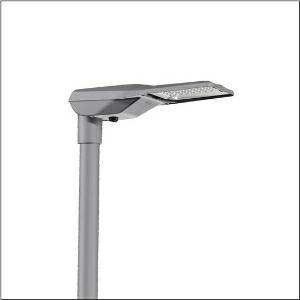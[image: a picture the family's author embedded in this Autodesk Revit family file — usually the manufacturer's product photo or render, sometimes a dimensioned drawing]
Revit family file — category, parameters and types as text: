
# Revit family: streetlight_sl_21_mini___p0_8a_5xe2u33r08hb_8bcd
name_source: partatom
category: Lighting Fixtures
units: mm (PartAtom-declared; Revit-internal decimal feet)

## family parameters
Cut with Voids When Loaded = No
Host = Face
Light Source = No
Part Type = Normal
Room Calculation Point = No
Round Connector Dimension = Use Diameter
Shared = No

## types (1)
- --- (1 x LED, 9120 lm, 66 W, 3000K)
    Apparent Load = 66 VA
    CIE Flux Codes = 33 69 96 100 100
    Color Rendering = 70
    Color Temperature = 3000K
    Default Elevation = 1800 mm
    Description = Streetlight SL 21 mini, mast luminaire, primary light control with lens, of PMMA, primary optical cover: cover, of toughened safety glass, transparent, light distribution: P0.8a, light emission: direct distribution, primary light characteristic: asymmetric, installation type: post-top, side-entry, LED, High Power LED, rated luminous flux: 9.120lm, luminous efficacy: 138lm/W, light colour: 730, colour temperature: 3000K, control gear: D4i, control: pre-setting: logarithmic dimming characteristic, flexible luminous flux parameterisation, time-dependent luminous flux control, constant luminous flux control, overheat protection, mains connection: 220..240V, AC, 50/60Hz, start of lifetime: 66W, end of service life: 69W, reduction: 30W, luminaire housing, of diecast aluminium, powder-coated, Siteco® metallic grey (DB 702S), corrosivity category C5 mid according to DIN EN ISO 12944, multi-level sealing system, sealing non-destructively replaceable, inclination adjustable: 0°, 5°, 10°, 15°, please order mast flange separately, length: 628mm, width: 235mm, height: 110mm, mast flange for spigot size: 42mm (side-entry): 5XC10008XM4, 60/48mm (side-entry/post-top): 5XC10108XM2, 76/60mm (side-entry/post-top): 5XC10108XM1, mounting height: 4..8m, Smart Interface below, protection rating (complete): IP66, insulation class (complete): insulation class II (safety insulation), certification: CE, ENEC, ENEC+, VDE, impact resistance: IK09, permissible operating ambient temperature for outdoor applications: -40..+50°C, standard-compliant lighting for roads and squares, packaging unit: 1 piece

Light Distribution: P0.8a
    Height = 110 mm
    Lamp = 1 x LED
    Lamp Light Flux = 9120 lm
    Lamp Power = 66 W
    Lamp count = 1
    Length = 625 mm
    Luminous efficacy = 138 lm/W
    Manufacturer = Siteco
    ModVariant = No
    Model = 5XE2U33R08HB
    Number of Poles = 1
    OnlyDefault = Yes
    Power Factor = 1
    Product Name = Streetlight SL 21 mini | P0.8a
    Product group = mast luminaire | pylon top
    ProductGroupID = 6100
    Protection Class = Protection class II
    Protection Degree = IP 66
    RLX_Detail_Level = 1
    RLX_Emergency_Light_Flux = 0 lm
    RLX_Emergency_Type = 0
    RLX_Emergency_Type_DB = No
    RlxData = <blob elided: 91941 chars, md5=da788405>
    Socket = socket
    Standby Power = 0 W
    System Light Flux = 9120 lm
    System Power = 66 W
    Type Comments = factory setting: luminous flux: 100 % | dim-lin: 254 | 670 mA
    Type Image = l_1003516.jpg
    URL = http://relux.com
    VarID = @adj_069518
    Voltage = 0 V
    Weight = 0.00 kg
    Width = 234 mm

## geometry (parser evidence)
native form markers: Blend x4, Sweep x11
no freeform markers — native parametric forms only
